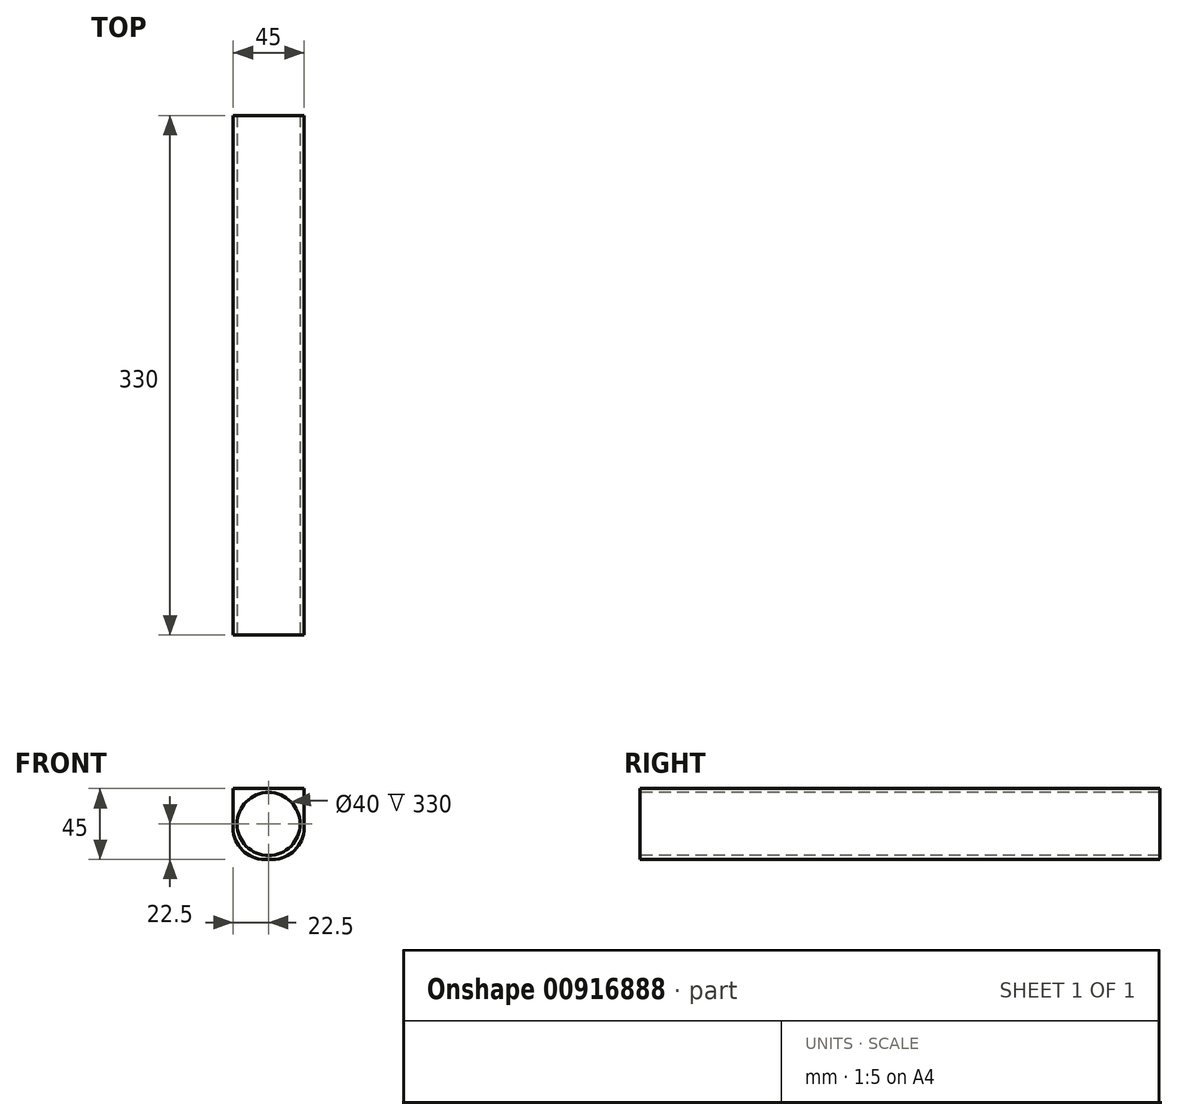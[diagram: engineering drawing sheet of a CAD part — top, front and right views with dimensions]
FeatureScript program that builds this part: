
annotation { "Feature Type Name" : "Feature", "Feature Type Description" : "" }
export const myFeature = defineFeature(function(context is Context, id is Id, definition is map)
    precondition{}
    {
        {
            var Q0;
            Q0=qCreatedBy(makeId("Front.planeOp"),FACE);
            var sketch = newSketch(context, id + "F0", { "sketchPlane" : qUnion([Q0])});
            skCircle(sketch, "E0", {"center": v(0, 0) * mm, "radius": 20 * mm});
            skLineSegment(sketch, "E1.bottom", {"start": v(22.5, 22.5) * mm, "end": v(-22.5, 22.5) * mm});
            skLineSegment(sketch, "E1.top", {"start": v(2.5, -22.5) * mm, "end": v(-2.5, -22.5) * mm});
            skLineSegment(sketch, "E1.left", {"start": v(22.5, 22.5) * mm, "end": v(22.5, -2.5) * mm});
            skLineSegment(sketch, "E1.right", {"start": v(-22.5, 22.5) * mm, "end": v(-22.5, -2.5) * mm});
            skPoint(sketch, "E2.visualSharp", {"position": v(-22.5, -22.5) * mm});
            skArc(sketch, "E2.filletArc", {"start": v(-22.5, -2.5) * mm, "mid": v(-16.64, -16.64) * mm, "end": v(-2.5, -22.5) * mm});
            skPoint(sketch, "E3.visualSharp", {"position": v(22.5, -22.5) * mm});
            skArc(sketch, "E3.filletArc", {"start": v(2.5, -22.5) * mm, "mid": v(16.64, -16.64) * mm, "end": v(22.5, -2.5) * mm});
            skSolve(sketch);
        }
        {
            var Q0;
            Q0=makeQuery(id+"F0.imprint","IMPRINT",FACE,{"disambiguationData":[TD([[makeQuery(id+"F0.imprint","IMPRINT",EDGE,{"derivedFrom":sQuery(id+"F0.wireOp",EDGE,"E0")}),-1.0]])]});
            extrude(context, id + "F1", {"entities" : qUnion([Q0]), "endBound" : BoundingType.SYMMETRIC, "oppositeDirection" : true, "depth" : 330 * mm, "offsetDistance" : 25 * mm});
        }
    });
